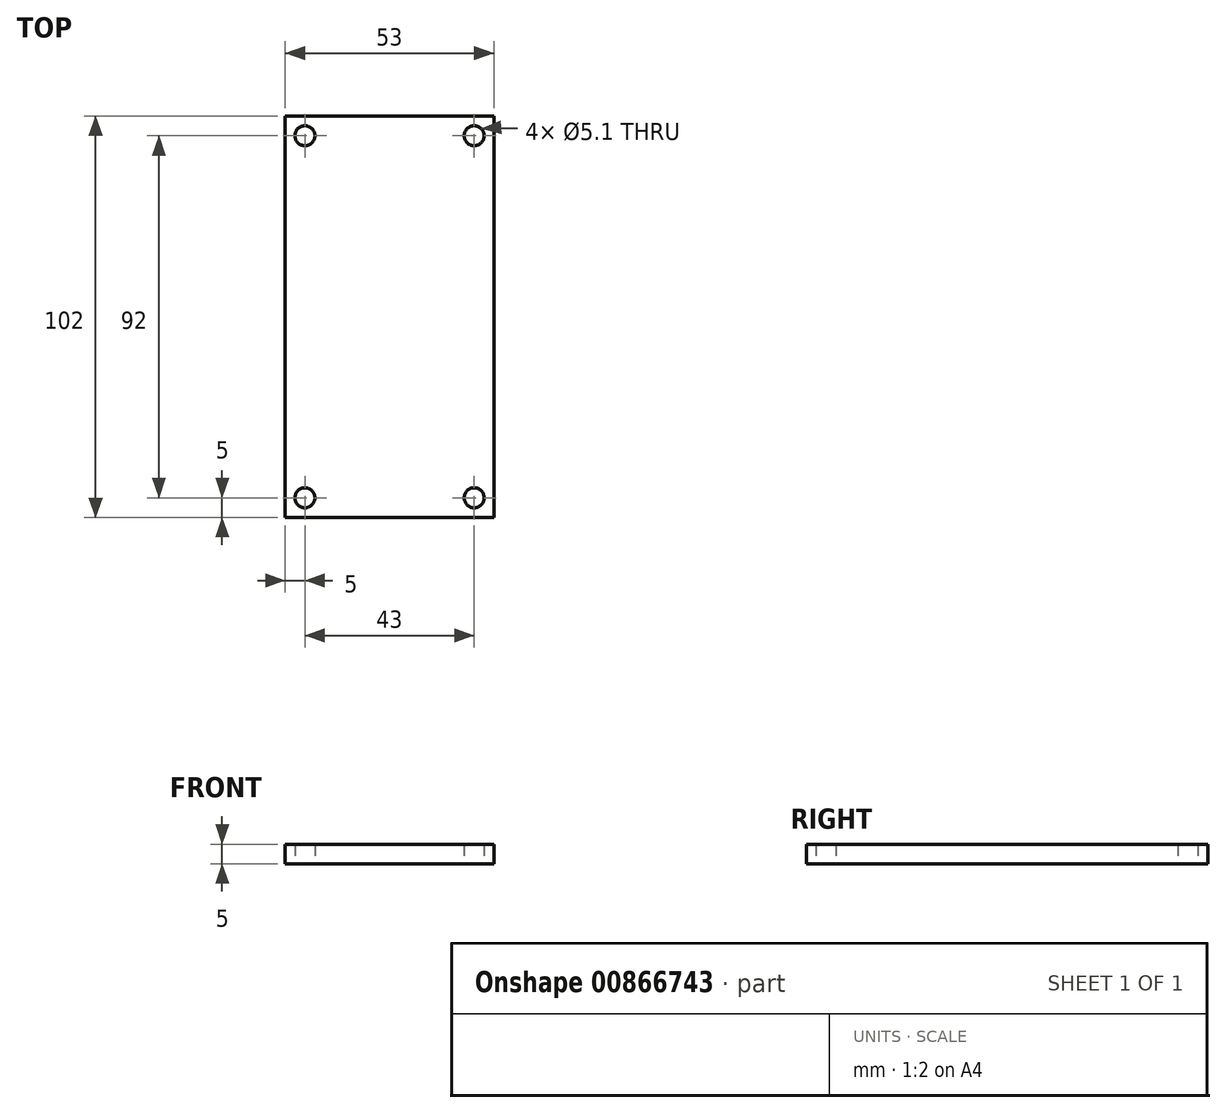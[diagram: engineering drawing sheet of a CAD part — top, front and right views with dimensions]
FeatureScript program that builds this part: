
annotation { "Feature Type Name" : "Feature", "Feature Type Description" : "" }
export const myFeature = defineFeature(function(context is Context, id is Id, definition is map)
    precondition{}
    {
        {
            var Q0;
            Q0=qCreatedBy(makeId("Top.planeOp"),FACE);
            var sketch = newSketch(context, id + "F0", { "sketchPlane" : qUnion([Q0])});
            skLineSegment(sketch, "E0.bottom", {"start": v(-26.5, 51) * mm, "end": v(26.5, 51) * mm});
            skLineSegment(sketch, "E0.top", {"start": v(-26.5, -51) * mm, "end": v(26.5, -51) * mm});
            skLineSegment(sketch, "E0.left", {"start": v(-26.5, 51) * mm, "end": v(-26.5, -51) * mm});
            skLineSegment(sketch, "E0.right", {"start": v(26.5, 51) * mm, "end": v(26.5, -51) * mm});
            skPoint(sketch, "E0.middle", {"position": v(0, 0) * mm});
            skLineSegment(sketch, "E1.bottom", {"start": v(-21.5, 46) * mm, "end": v(21.5, 46) * mm});
            skLineSegment(sketch, "E1.top", {"start": v(-21.5, -46) * mm, "end": v(21.5, -46) * mm});
            skLineSegment(sketch, "E1.left", {"start": v(-21.5, 46) * mm, "end": v(-21.5, -46) * mm});
            skLineSegment(sketch, "E1.right", {"start": v(21.5, 46) * mm, "end": v(21.5, -46) * mm});
            skCircle(sketch, "E2", {"center": v(-21.5, 46) * mm, "radius": 2.55 * mm});
            skCircle(sketch, "E3", {"center": v(21.5, 46) * mm, "radius": 2.55 * mm});
            skCircle(sketch, "E4", {"center": v(-21.5, -46) * mm, "radius": 2.55 * mm});
            skCircle(sketch, "E5", {"center": v(21.5, -46) * mm, "radius": 2.55 * mm});
            skLineSegment(sketch, "E6", {"start": v(-26.5, 51) * mm, "end": v(26.5, -51) * mm});
            skLineSegment(sketch, "E7", {"start": v(26.5, 51) * mm, "end": v(-26.5, -51) * mm});
            skSolve(sketch);
        }
        {
            var Q0;
            Q0 = qSketchRegion(id + "F0", true);
            var Q1;
            {var subQ0=sQuery(id+"F0.wireOp",EDGE,"E4");var subQ1=sQuery(id+"F0.wireOp",EDGE,"E1.top");var subQ2=makeQuery(id+"F0.imprint","INTERSECT",VERTEX,{"derivedFrom":[subQ1,subQ0]});Q1=makeQuery(id+"F0.imprint","IMPRINT",FACE,{"disambiguationData":[TD([[makeQuery(id+"F0.imprint","IMPRINT",EDGE,{"disambiguationData":[TD([[subQ2,-1.0]])],"derivedFrom":subQ1}),1.0]])]});}
            var Q2;
            {var subQ0=sQuery(id+"F0.wireOp",EDGE,"E7");var subQ1=sQuery(id+"F0.wireOp",EDGE,"E1.right");var subQ2=makeQuery(id+"F0.imprint","INTERSECT",VERTEX,{"derivedFrom":[subQ1,subQ0]});Q2=makeQuery(id+"F0.imprint","IMPRINT",FACE,{"disambiguationData":[TD([[makeQuery(id+"F0.imprint","IMPRINT",EDGE,{"disambiguationData":[TD([[subQ2,-1.0]])],"derivedFrom":subQ1}),-1.0]])]});}
            var Q3;
            {var subQ0=sQuery(id+"F0.wireOp",EDGE,"E2");var subQ1=sQuery(id+"F0.wireOp",EDGE,"E1.bottom");var subQ2=makeQuery(id+"F0.imprint","INTERSECT",VERTEX,{"derivedFrom":[subQ1,subQ0]});Q3=makeQuery(id+"F0.imprint","IMPRINT",FACE,{"disambiguationData":[TD([[makeQuery(id+"F0.imprint","IMPRINT",EDGE,{"disambiguationData":[TD([[subQ2,-1.0]])],"derivedFrom":subQ1}),-1.0]])]});}
            var Q4;
            {var subQ0=sQuery(id+"F0.wireOp",EDGE,"E6");var subQ1=sQuery(id+"F0.wireOp",EDGE,"E1.left");var subQ2=makeQuery(id+"F0.imprint","INTERSECT",VERTEX,{"derivedFrom":[subQ1,subQ0]});Q4=makeQuery(id+"F0.imprint","IMPRINT",FACE,{"disambiguationData":[TD([[makeQuery(id+"F0.imprint","IMPRINT",EDGE,{"disambiguationData":[TD([[subQ2,-1.0]])],"derivedFrom":subQ1}),1.0]])]});}
            var Q5;
            {var subQ0=sQuery(id+"F0.wireOp",EDGE,"E6");var subQ1=sQuery(id+"F0.wireOp",EDGE,"E1.right");var subQ2=makeQuery(id+"F0.imprint","INTERSECT",VERTEX,{"derivedFrom":[subQ1,subQ0]});Q5=makeQuery(id+"F0.imprint","IMPRINT",FACE,{"disambiguationData":[TD([[makeQuery(id+"F0.imprint","IMPRINT",EDGE,{"disambiguationData":[TD([[subQ2,-1.0]])],"derivedFrom":subQ1}),1.0]])]});}
            var Q6;
            {var subQ0=sQuery(id+"F0.wireOp",EDGE,"E7");var subQ1=sQuery(id+"F0.wireOp",EDGE,"E1.left");var subQ2=makeQuery(id+"F0.imprint","INTERSECT",VERTEX,{"derivedFrom":[subQ1,subQ0]});Q6=makeQuery(id+"F0.imprint","IMPRINT",FACE,{"disambiguationData":[TD([[makeQuery(id+"F0.imprint","IMPRINT",EDGE,{"disambiguationData":[TD([[subQ2,-1.0]])],"derivedFrom":subQ1}),-1.0]])]});}
            var Q7;
            {var subQ0=sQuery(id+"F0.wireOp",EDGE,"E3");var subQ1=sQuery(id+"F0.wireOp",EDGE,"E1.right");var subQ2=makeQuery(id+"F0.imprint","INTERSECT",VERTEX,{"derivedFrom":[subQ1,subQ0]});Q7=makeQuery(id+"F0.imprint","IMPRINT",FACE,{"disambiguationData":[TD([[makeQuery(id+"F0.imprint","IMPRINT",EDGE,{"disambiguationData":[TD([[subQ2,-1.0]])],"derivedFrom":subQ1}),1.0]])]});}
            var Q8;
            {var subQ0=sQuery(id+"F0.wireOp",EDGE,"E2");var subQ1=sQuery(id+"F0.wireOp",EDGE,"E1.left");var subQ2=makeQuery(id+"F0.imprint","INTERSECT",VERTEX,{"derivedFrom":[subQ1,subQ0]});Q8=makeQuery(id+"F0.imprint","IMPRINT",FACE,{"disambiguationData":[TD([[makeQuery(id+"F0.imprint","IMPRINT",EDGE,{"disambiguationData":[TD([[subQ2,-1.0]])],"derivedFrom":subQ1}),-1.0]])]});}
            extrude(context, id + "F1", {"entities" : qUnion([Q0, Q1, Q2, Q3, Q4, Q5, Q6, Q7, Q8]), "depth" : 5 * mm, "offsetDistance" : 25 * mm});
        }
    });
